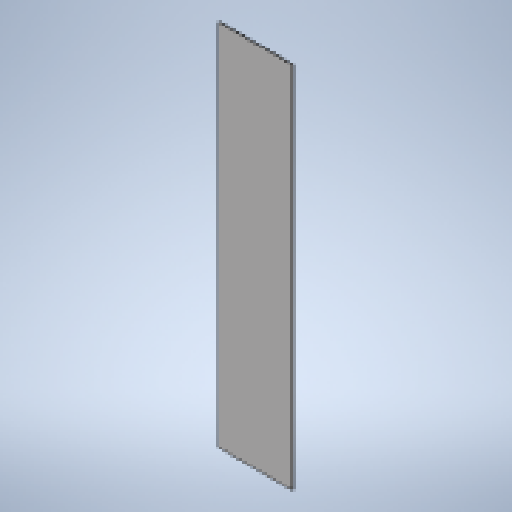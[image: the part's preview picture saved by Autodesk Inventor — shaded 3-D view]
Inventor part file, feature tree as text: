
AUTODESK INVENTOR PART (.ipt)
format: ipt  version: 2025 (Build 290162010, 162A)  size: 138,752 bytes
history: native  units: mm
features: sheet_metal_op x1, sketch x1, other x1
ambient origin geometry x8: Origin, YZ Plane, XZ Plane, XY Plane, X Axis, Y Axis, Z Axis, Center Point
bodies: Solid1 (feature_tree)
feature tree (3):
  sheet_metal_op  "Face1"
  sketch  "Sketch1"  dims[d0=200.0mm d1=1250.0mm d2=2.0mm]
  other  "Plate1"
